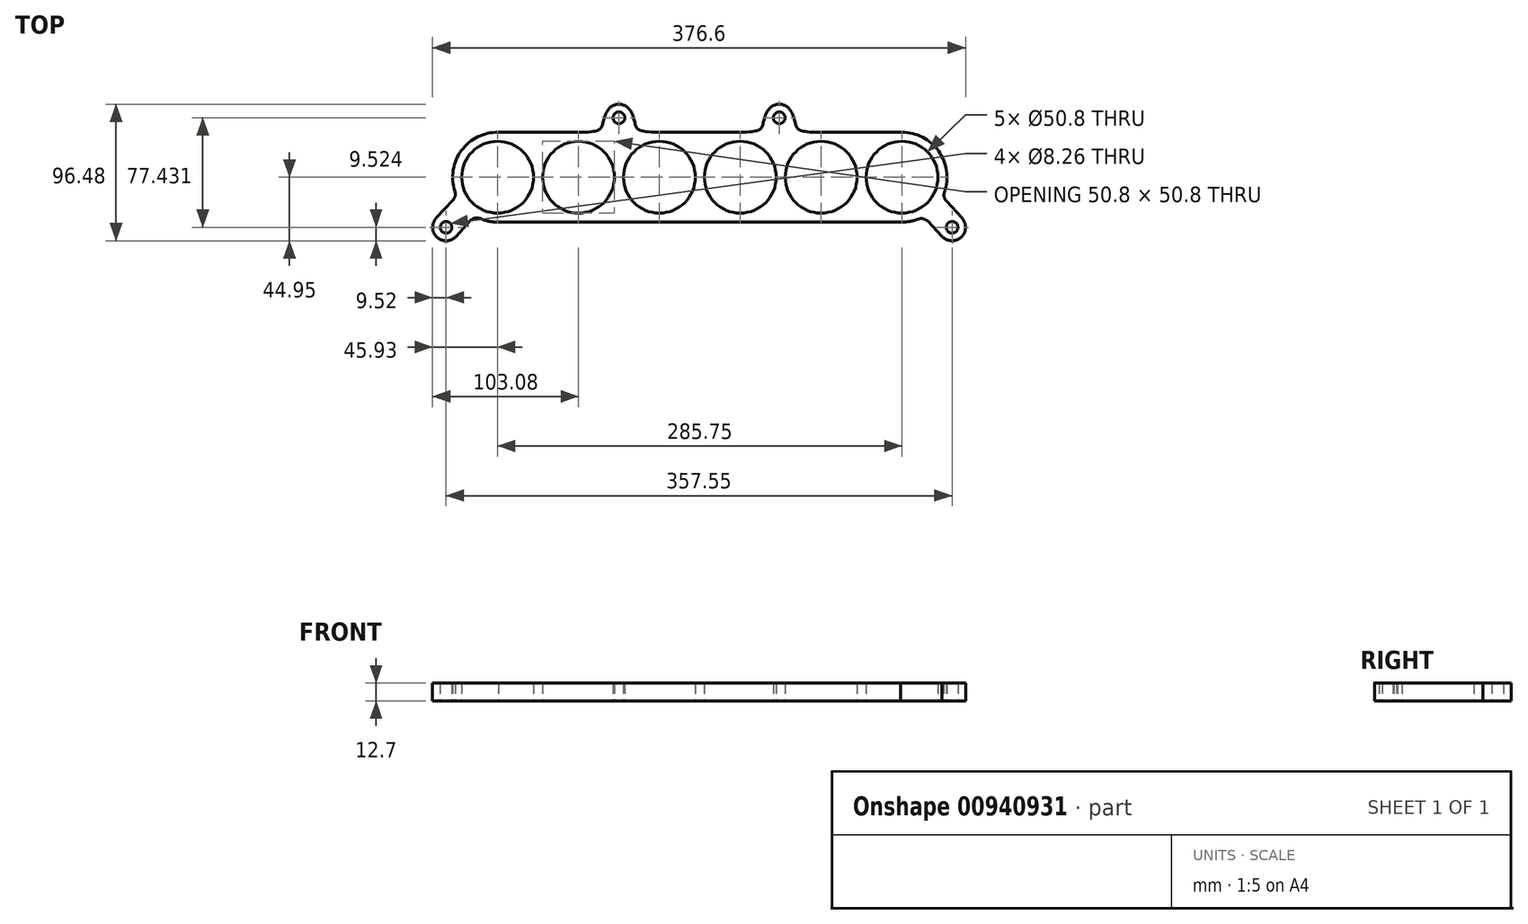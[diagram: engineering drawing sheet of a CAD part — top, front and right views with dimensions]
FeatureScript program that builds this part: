
annotation { "Feature Type Name" : "Feature", "Feature Type Description" : "" }
export const myFeature = defineFeature(function(context is Context, id is Id, definition is map)
    precondition{}
    {
        {
            var Q0;
            Q0=qCreatedBy(makeId("Top.planeOp"),FACE);
            var sketch = newSketch(context, id + "F0", { "sketchPlane" : qUnion([Q0])});
            skCircle(sketch, "E0", {"center": v(-172.95, 0) * mm, "radius": 25.4 * mm});
            skCircle(sketch, "E1.1.0.0", {"center": v(-115.8, 0) * mm, "radius": 25.4 * mm});
            skCircle(sketch, "E1.2.0.0", {"center": v(-58.65, 0) * mm, "radius": 25.4 * mm});
            skCircle(sketch, "E1.3.0.0", {"center": v(-1.5, 0) * mm, "radius": 25.4 * mm});
            skCircle(sketch, "E1.4.0.0", {"center": v(55.65, 0) * mm, "radius": 25.4 * mm});
            skCircle(sketch, "E1.5.0.0", {"center": v(112.8, 0) * mm, "radius": 25.4 * mm});
            skLineSegment(sketch, "E1.direction1", {"start": v(-172.95, 0) * mm, "end": v(-115.8, 0) * mm, "construction": true});
            skArc(sketch, "E2", {"start": v(-141.2, -0.02) * mm, "mid": v(-141.2, 0) * mm, "end": v(-141.2, 0.02) * mm});
            skArc(sketch, "E3", {"start": v(111.78, -31.73) * mm, "mid": v(118.08, -31.3) * mm, "end": v(124.17, -29.65) * mm});
            skLineSegment(sketch, "E4", {"start": v(-173.69, 31.74) * mm, "end": v(-116.09, 31.74) * mm});
            skLineSegment(sketch, "E5", {"start": v(111.78, -31.73) * mm, "end": v(-172.95, -31.75) * mm});
            skArc(sketch, "E6.trimOffspring", {"start": v(-172.21, 31.74) * mm, "mid": v(-198.43, 18.94) * mm, "end": v(-203.13, -9.85) * mm});
            skCircle(sketch, "E7", {"center": v(-87.23, 42) * mm, "radius": 4.13 * mm});
            skArc(sketch, "E8", {"start": v(-78.82, 46.47) * mm, "mid": v(-87.23, 51.53) * mm, "end": v(-95.64, 46.47) * mm});
            skFitSpline(sketch, "E9", {"points": [v(-95.64, 46.47) * mm, v(-116.09, 31.74) * mm], "startDerivative": vector(-17.93, -33.71) * mm, "endDerivative": vector(-65.88, 0) * mm});
            skFitSpline(sketch, "E10.MirrorCS", {"points": [v(-78.82, 46.47) * mm, v(-58.36, 31.74) * mm], "startDerivative": vector(17.93, -33.71) * mm, "endDerivative": vector(65.88, 0) * mm});
            skLineSegment(sketch, "E11.trimOffspring", {"start": v(-59.18, 31.74) * mm, "end": v(-2, 31.75) * mm});
            skFitSpline(sketch, "E12.MirrorCS", {"points": [v(17.64, 46.48) * mm, v(-2.8, 31.74) * mm], "startDerivative": vector(-17.93, -33.71) * mm, "endDerivative": vector(-65.88, 0) * mm});
            skArc(sketch, "E13.MirrorCS", {"start": v(17.64, 46.48) * mm, "mid": v(26.05, 51.53) * mm, "end": v(34.46, 46.48) * mm});
            skFitSpline(sketch, "E14.MirrorCS", {"points": [v(34.46, 46.48) * mm, v(54.91, 31.75) * mm], "startDerivative": vector(17.93, -33.71) * mm, "endDerivative": vector(65.88, 0) * mm});
            skCircle(sketch, "E15.MirrorC", {"center": v(26.05, 42) * mm, "radius": 4.13 * mm});
            skLineSegment(sketch, "E16.trimOffspring", {"start": v(54.91, 31.75) * mm, "end": v(112.8, 31.75) * mm});
            skArc(sketch, "E17", {"start": v(141.17, -41.84) * mm, "mid": v(154.64, -42.41) * mm, "end": v(155.19, -28.94) * mm});
            skCircle(sketch, "E18", {"center": v(148.2, -35.4) * mm, "radius": 4.13 * mm});
            skLineSegment(sketch, "E19", {"start": v(155.19, -28.94) * mm, "end": v(144.09, -16.92) * mm});
            skLineSegment(sketch, "E20", {"start": v(141.41, -42.1) * mm, "end": v(131.04, -31.2) * mm});
            skArc(sketch, "E21.trimOffspring", {"start": v(142.76, -10.51) * mm, "mid": v(138.7, 18.36) * mm, "end": v(112.8, 31.75) * mm});
            skPoint(sketch, "E22.visualSharp", {"position": v(127.92, -27.92) * mm});
            skArc(sketch, "E22.filletArc", {"start": v(131.04, -31.2) * mm, "mid": v(127.84, -29.38) * mm, "end": v(124.17, -29.65) * mm});
            skPoint(sketch, "E23.visualSharp", {"position": v(141.33, -13.93) * mm});
            skArc(sketch, "E23.filletArc", {"start": v(142.76, -10.51) * mm, "mid": v(142.53, -13.9) * mm, "end": v(144.09, -16.92) * mm});
            skPoint(sketch, "E24.startSnap0", {"position": v(-30.58, -31.74) * mm});
            skLineSegment(sketch, "E25", {"start": v(-30.58, -31.74) * mm, "end": v(-30.58, -61.55) * mm});
            skArc(sketch, "E26.MirrorCS", {"start": v(-202.34, -41.86) * mm, "mid": v(-215.8, -42.44) * mm, "end": v(-216.36, -28.97) * mm});
            skCircle(sketch, "E27.MirrorC", {"center": v(-209.36, -35.43) * mm, "radius": 4.13 * mm});
            skLineSegment(sketch, "E28", {"start": v(-216.36, -28.97) * mm, "end": v(-204.5, -16.13) * mm});
            skLineSegment(sketch, "E29", {"start": v(-202.34, -41.86) * mm, "end": v(-192.27, -30.88) * mm});
            skArc(sketch, "E30.trimOffspring", {"start": v(-185.15, -29.31) * mm, "mid": v(-179.17, -31.14) * mm, "end": v(-172.95, -31.75) * mm});
            skPoint(sketch, "E31.visualSharp", {"position": v(-201.82, -13.22) * mm});
            skArc(sketch, "E31.filletArc", {"start": v(-204.5, -16.13) * mm, "mid": v(-202.97, -13.17) * mm, "end": v(-203.13, -9.85) * mm});
            skPoint(sketch, "E32.visualSharp", {"position": v(-189.04, -27.37) * mm});
            skArc(sketch, "E32.filletArc", {"start": v(-185.15, -29.31) * mm, "mid": v(-188.96, -28.97) * mm, "end": v(-192.27, -30.88) * mm});
            skLineSegment(sketch, "E33", {"start": v(-209.36, -35.43) * mm, "end": v(-172.95, 0) * mm});
            skSolve(sketch);
        }
        {
            var Q0;
            Q0 = qSketchRegion(id + "F0", true);
            extrude(context, id + "F1", {"entities" : qUnion([Q0]), "depth" : 12.7 * mm, "offsetDistance" : 25.4 * mm});
        }
    });
